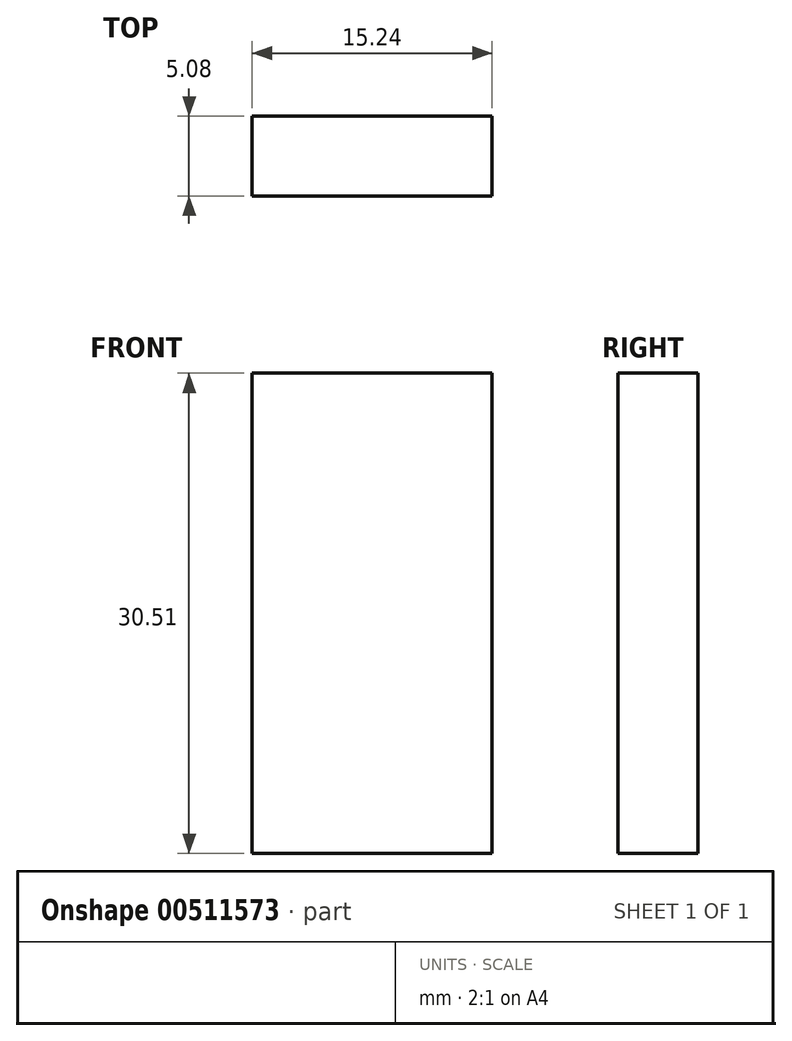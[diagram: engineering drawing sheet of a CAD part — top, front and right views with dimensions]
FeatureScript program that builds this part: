
annotation { "Feature Type Name" : "Feature", "Feature Type Description" : "" }
export const myFeature = defineFeature(function(context is Context, id is Id, definition is map)
    precondition{}
    {
        {
            var Q0;
            Q0=qCreatedBy(makeId("Front.planeOp"),FACE);
            var sketch = newSketch(context, id + "F0", { "sketchPlane" : qUnion([Q0])});
            skLineSegment(sketch, "E0", {"start": v(0, 0) * mm, "end": v(-15.24, 0) * mm});
            skLineSegment(sketch, "E1", {"start": v(-15.24, 0) * mm, "end": v(-15.24, 30.5) * mm});
            skLineSegment(sketch, "E2", {"start": v(-15.24, 30.5) * mm, "end": v(0, 30.5) * mm});
            skLineSegment(sketch, "E3", {"start": v(0, 30.5) * mm, "end": v(0, 0) * mm});
            skSolve(sketch);
        }
        {
            var Q0;
            Q0 = qSketchRegion(id + "F0", true);
            extrude(context, id + "F1", {"entities" : qUnion([Q0]), "depth" : 5.08 * mm, "offsetDistance" : 25.4 * mm});
        }
    });
